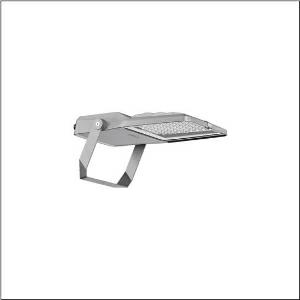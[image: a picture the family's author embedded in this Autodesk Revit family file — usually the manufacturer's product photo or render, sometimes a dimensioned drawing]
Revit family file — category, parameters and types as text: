
# Revit family: floodlight_fl_21_iq_mini___pl52_5xa7771c4d1a_1f8c
name_source: partatom
category: Lighting Fixtures
units: mm (PartAtom-declared; Revit-internal decimal feet)

## family parameters
Cut with Voids When Loaded = No
Host = Face
Light Source = No
Part Type = Normal
Room Calculation Point = No
Round Connector Dimension = Use Diameter
Shared = No

## types (1)
- --- (1 x LED, 12720 lm, 87.2 W, 4000K)
    Apparent Load = 87 VA
    CIE Flux Codes = 26 60 98 100 100
    Color Rendering = 70
    Color Temperature = 4000K
    Default Elevation = 1800 mm
    Description = Floodlight FL 21 iQ mini, floodlight, primary light control with lens, of PMMA, primary optical cover: protective disc, of toughened safety glass, transparent, light distribution: PL52, light emission: direct distribution, installation type: surface-mounted, lamps: LED, High Power LED, rated values: 12.720lm | 87,2W | 145,9lm/W (begin service life); end service life: 12.720lm | 92,1W; at 50% lumin. flux: 6.360lm | 40,2W | 158,2lm/W, colour temperature: 4000K, colour rendering: CRI > 70, light colour: 740, light setting 1 begin service life: 100% | 12.720lm | 87,2W | 145,9lm/W | 4.000K, light setting 1 end service life: 92,1W, further light settings possible, control: Auto-Match, Temp-Guard, Lumen-Switch, Night-Set, Smart-Wire, Light-Fading, Desk-Remote (wireless, voltage-free reading and setting of iQ features in the workshop via application-optimized NFC function/RFID function), optimised constant luminous flux control (CLO 2.0), pre-setting: linear dimming characteristic, with terminal, 6-pole, mains connection: 220..240V, AC, 50/60Hz, luminaire housing, of diecast aluminium, powder-coated, SITECO metallic grey (DB 702S), corrosivity category C5 mid according to DIN EN ISO 12944suitable for swimming poolschlorine-resistant, sealing non-destructively replaceable, mounting bracket, of steel, galvanised, powder-coated, SITECO metallic grey (DB 702S), protection rating (complete): IP66, insulation class (complete): insulation class II (safety insulation), certification: CE, ENEC, VDE, protection symbol: D, impact resistance: IK08, permissible operating ambient temperature: -40..+40°C, permissible operating ambient temperature for outdoor applications: -40..+50°C, standard: DIN EN 12944, LABS conformity tested according to VDMA 24364:2018-05, packaging unit: 1 piece

Light Distribution: PL52
    Height = 70 mm
    Lamp = 1 x LED
    Lamp Light Flux = 12720 lm
    Lamp Power = 87.2 W
    Lamp count = 1
    Length = 485 mm
    Luminous efficacy = 146 lm/W
    Manufacturer = Siteco
    ModVariant = No
    Model = 5XA7771C4D1A
    Number of Poles = 1
    OnlyDefault = Yes
    Power Factor = 1
    Product Name = Floodlight FL 21 iQ mini | PL52
    Product group = floodlight | pylon annexe
    ProductGroupID = 6201
    Protection Class = Protection class II
    Protection Degree = IP 66
    RLX_Detail_Level = 1
    RLX_Emergency_Light_Flux = 0 lm
    RLX_Emergency_Type = 0
    RLX_Emergency_Type_DB = No
    RlxData = <blob elided: 96789 chars, md5=85a1afa3>
    Socket = socket
    Standby Power = 0 W
    System Light Flux = 12720 lm
    System Power = 87 W
    Type Comments = factory setting: luminous flux: 100 % | dim-lin: 254 | 456 mA
    Type Image = l_1006845.jpg
    URL = http://relux.com
    VarID = @adj_163989
    Voltage = 0 V
    Weight = 0.00 kg
    Width = 337 mm

## geometry (parser evidence)
native form markers: Blend x4, Sweep x11
no freeform markers — native parametric forms only
